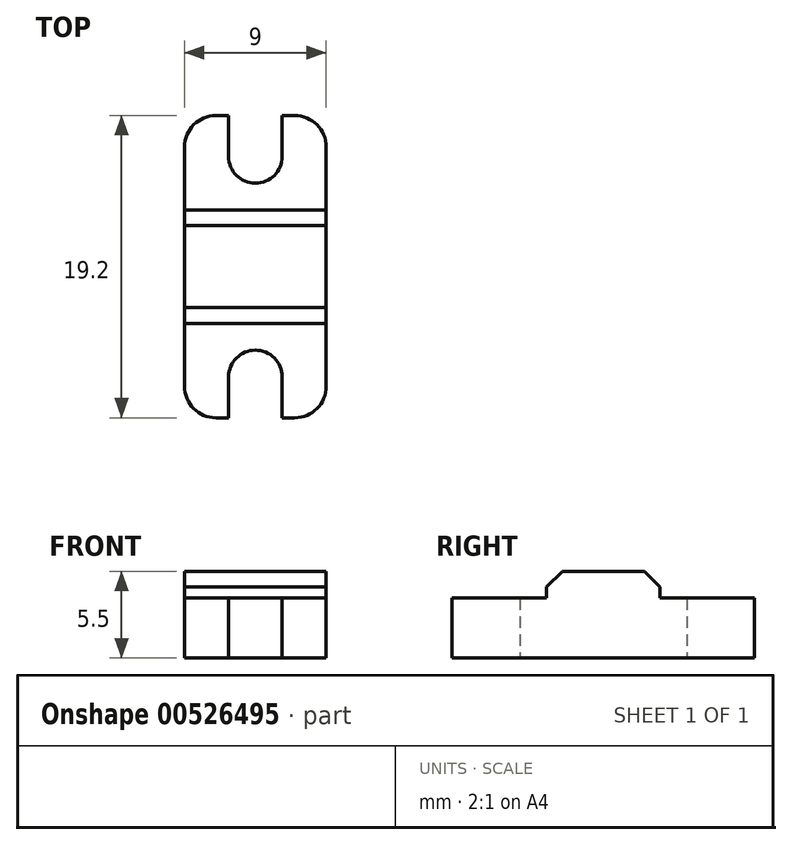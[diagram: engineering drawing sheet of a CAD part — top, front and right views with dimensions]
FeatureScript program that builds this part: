
annotation { "Feature Type Name" : "Feature", "Feature Type Description" : "" }
export const myFeature = defineFeature(function(context is Context, id is Id, definition is map)
    precondition{}
    {
        {
            var Q0;
            Q0=qCreatedBy(makeId("Top.planeOp"),FACE);
            var sketch = newSketch(context, id + "F0", { "sketchPlane" : qUnion([Q0])});
            skLineSegment(sketch, "E0", {"start": v(4.5, 0) * mm, "end": v(4.5, -7.6) * mm});
            skLineSegment(sketch, "E1", {"start": v(2.5, -9.6) * mm, "end": v(1.7, -9.6) * mm});
            skLineSegment(sketch, "E2", {"start": v(1.7, -9.6) * mm, "end": v(1.7, -7) * mm});
            skArc(sketch, "E3", {"start": v(1.7, -7) * mm, "mid": v(1.2, -5.8) * mm, "end": v(0, -5.3) * mm});
            skLineSegment(sketch, "E4", {"start": v(0, -5.3) * mm, "end": v(0, 0) * mm});
            skLineSegment(sketch, "E5", {"start": v(4.5, 0) * mm, "end": v(0, 0) * mm});
            skPoint(sketch, "E6.visualSharp", {"position": v(4.5, -9.6) * mm});
            skArc(sketch, "E6.filletArc", {"start": v(2.5, -9.6) * mm, "mid": v(3.91, -9.01) * mm, "end": v(4.5, -7.6) * mm});
            skSolve(sketch);
        }
        {
            var Q0;
            Q0 = qSketchRegion(id + "F0", true);
            extrude(context, id + "F1", {"entities" : qUnion([Q0]), "depth" : 3.8 * mm, "offsetDistance" : 25 * mm});
        }
        {
            var Q0;
            Q0=makeQuery(id+"F1.opExtrude","SWEPT_FACE",FACE,{"disambiguationData":[OSD([sQuery(id+"F0.wireOp",EDGE,"E0")])]});
            var sketch = newSketch(context, id + "F2", { "sketchPlane" : qUnion([Q0])});
            skLineSegment(sketch, "E7", {"start": v(-3.6, 3.8) * mm, "end": v(-3.6, 4.5) * mm});
            skLineSegment(sketch, "E8", {"start": v(-3.6, 4.5) * mm, "end": v(-2.6, 5.5) * mm});
            skLineSegment(sketch, "E9", {"start": v(-2.6, 5.5) * mm, "end": v(0, 5.5) * mm});
            skLineSegment(sketch, "E10", {"start": v(0, 5.5) * mm, "end": v(0, 3.8) * mm});
            skLineSegment(sketch, "E11", {"start": v(0, 3.8) * mm, "end": v(-3.6, 3.8) * mm});
            skSolve(sketch);
        }
        {
            var Q0;
            Q0 = qSketchRegion(id + "F2", true);
            var Q1;
            Q1=makeQuery(id+"F1.opExtrude","SWEPT_FACE",FACE,{"disambiguationData":[OSD([sQuery(id+"F0.wireOp",EDGE,"E4")])]});
            extrude(context, id + "F3", {"entities" : qUnion([Q0]), "operationType" : NewBodyOperationType.ADD, "endBound" : BoundingType.UP_TO_SURFACE, "oppositeDirection" : true, "depth" : 25 * mm, "endBoundEntityFace" : qUnion([Q1]), "offsetDistance" : 25 * mm});
        }
        {
            var Q0;
            Q0=makeQuery(id+"F1.opExtrude","SWEPT_BODY",BODY,{"disambiguationData":[OSD([sQuery(id+"F0.wireOp",EDGE,"E0"),sQuery(id+"F0.wireOp",EDGE,"E1"),sQuery(id+"F0.wireOp",EDGE,"E2"),sQuery(id+"F0.wireOp",EDGE,"E3"),sQuery(id+"F0.wireOp",EDGE,"E4"),sQuery(id+"F0.wireOp",EDGE,"E5"),sQuery(id+"F0.wireOp",EDGE,"E6.filletArc")])]});
            var Q1;
            {var subQ0=sQuery(id+"F0.wireOp",EDGE,"E4");Q1=makeQuery(id+"F3.boolean.opBoolean","MERGE",FACE,{"derivedFrom":[makeQuery(id+"F1.opExtrude","SWEPT_FACE",FACE,{"disambiguationData":[OSD([subQ0])]}),makeQuery(id+"F3.opExtrude","CAP_FACE",FACE,{"disambiguationData":[OSD([subQ0])],"isStart":false})]});}
            mirror(context, id + "F4", {"operationType" : NewBodyOperationType.ADD, "entities" : qUnion([Q0]), "mirrorPlane" : qUnion([Q1])});
        }
        {
            var Q0;
            Q0=makeQuery(id+"F1.opExtrude","SWEPT_BODY",BODY,{"disambiguationData":[OSD([sQuery(id+"F0.wireOp",EDGE,"E0"),sQuery(id+"F0.wireOp",EDGE,"E1"),sQuery(id+"F0.wireOp",EDGE,"E2"),sQuery(id+"F0.wireOp",EDGE,"E3"),sQuery(id+"F0.wireOp",EDGE,"E4"),sQuery(id+"F0.wireOp",EDGE,"E5"),sQuery(id+"F0.wireOp",EDGE,"E6.filletArc")])]});
            var Q1;
            {var subQ0=makeQuery(id+"F3.boolean.opBoolean","MERGE",FACE,{"derivedFrom":[makeQuery(id+"F1.opExtrude","SWEPT_FACE",FACE,{"disambiguationData":[OSD([sQuery(id+"F0.wireOp",EDGE,"E5")])]}),makeQuery(id+"F3.opExtrude","SWEPT_FACE",FACE,{"disambiguationData":[OSD([sQuery(id+"F2.wireOp",EDGE,"E10")])]})]});Q1=makeQuery(id+"F4.boolean.opBoolean","MERGE",FACE,{"derivedFrom":[subQ0,makeQuery(id+"F4.opPattern","COPY",FACE,{"derivedFrom":subQ0,"instanceName":"1"})]});}
            mirror(context, id + "F5", {"operationType" : NewBodyOperationType.ADD, "entities" : qUnion([Q0]), "mirrorPlane" : qUnion([Q1])});
        }
    });
